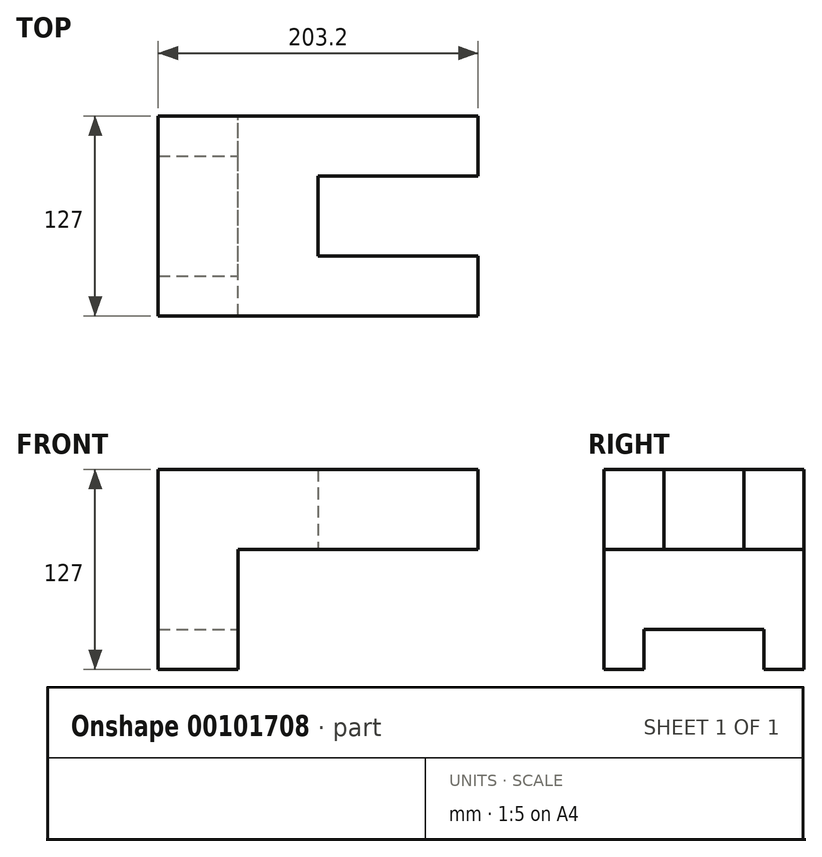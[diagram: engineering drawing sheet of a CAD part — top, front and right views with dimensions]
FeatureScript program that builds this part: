
annotation { "Feature Type Name" : "Feature", "Feature Type Description" : "" }
export const myFeature = defineFeature(function(context is Context, id is Id, definition is map)
    precondition{}
    {
        {
            var Q0;
            Q0=qCreatedBy(makeId("Top.planeOp"),FACE);
            var sketch = newSketch(context, id + "F0", { "sketchPlane" : qUnion([Q0])});
            skLineSegment(sketch, "E0", {"start": v(-106.5, 62.7) * mm, "end": v(96.7, 62.7) * mm});
            skLineSegment(sketch, "E1", {"start": v(96.7, 62.7) * mm, "end": v(96.7, 24.6) * mm});
            skLineSegment(sketch, "E2", {"start": v(96.7, 24.6) * mm, "end": v(-4.9, 24.6) * mm});
            skLineSegment(sketch, "E3", {"start": v(-4.9, 24.6) * mm, "end": v(-4.9, -26.2) * mm});
            skLineSegment(sketch, "E4", {"start": v(-4.9, -26.2) * mm, "end": v(96.7, -26.2) * mm});
            skLineSegment(sketch, "E5", {"start": v(96.7, -26.2) * mm, "end": v(96.7, -64.3) * mm});
            skLineSegment(sketch, "E6", {"start": v(-106.5, 62.7) * mm, "end": v(-106.5, -64.3) * mm});
            skLineSegment(sketch, "E7", {"start": v(-106.5, -64.3) * mm, "end": v(96.7, -64.3) * mm});
            skSolve(sketch);
        }
        {
            var Q0;
            Q0 = qSketchRegion(id + "F0", true);
            var Q1;
            Q1=makeQuery(id+"F0.imprint","IMPRINT",FACE,{"disambiguationData":[TD([[makeQuery(id+"F0.imprint","IMPRINT",EDGE,{"derivedFrom":sQuery(id+"F0.wireOp",EDGE,"E0")}),-1.0]])]});
            extrude(context, id + "F1", {"entities" : qUnion([Q0, Q1]), "depth" : 50.8 * mm});
        }
        {
            var Q0;
            Q0=makeQuery(id+"F1.opExtrude","CAP_FACE",FACE,{"disambiguationData":[OSD([sQuery(id+"F0.wireOp",EDGE,"E0"),sQuery(id+"F0.wireOp",EDGE,"E1"),sQuery(id+"F0.wireOp",EDGE,"E2"),sQuery(id+"F0.wireOp",EDGE,"E3"),sQuery(id+"F0.wireOp",EDGE,"E4"),sQuery(id+"F0.wireOp",EDGE,"E5"),sQuery(id+"F0.wireOp",EDGE,"E6"),sQuery(id+"F0.wireOp",EDGE,"E7")])],"isStart":true});
            var sketch = newSketch(context, id + "F2", { "sketchPlane" : qUnion([Q0])});
            skLineSegment(sketch, "E8.bottom", {"start": v(-106.5, 64.3) * mm, "end": v(-55.7, 64.3) * mm});
            skLineSegment(sketch, "E8.top", {"start": v(-106.5, -62.7) * mm, "end": v(-55.7, -62.7) * mm});
            skLineSegment(sketch, "E8.left", {"start": v(-106.5, 64.3) * mm, "end": v(-106.5, -62.7) * mm});
            skLineSegment(sketch, "E8.right", {"start": v(-55.7, 64.3) * mm, "end": v(-55.7, -62.7) * mm});
            skSolve(sketch);
        }
        {
            var Q0;
            Q0=makeQuery(id+"F2.imprint","IMPRINT",FACE,{"disambiguationData":[TD([[makeQuery(id+"F2.imprint","IMPRINT",EDGE,{"derivedFrom":sQuery(id+"F2.wireOp",EDGE,"E8.bottom")}),-1.0]])]});
            extrude(context, id + "F3", {"entities" : qUnion([Q0]), "operationType" : NewBodyOperationType.ADD, "depth" : 50.8 * mm});
        }
        {
            var Q0;
            Q0=makeQuery(id+"F3.opExtrude","CAP_FACE",FACE,{"disambiguationData":[OSD([sQuery(id+"F2.wireOp",EDGE,"E8.bottom"),sQuery(id+"F2.wireOp",EDGE,"E8.top"),sQuery(id+"F2.wireOp",EDGE,"E8.left"),sQuery(id+"F2.wireOp",EDGE,"E8.right")])],"isStart":false});
            var sketch = newSketch(context, id + "F4", { "sketchPlane" : qUnion([Q0])});
            skLineSegment(sketch, "E9.bottom", {"start": v(-106.5, -62.7) * mm, "end": v(-55.7, -62.7) * mm});
            skLineSegment(sketch, "E9.top", {"start": v(-106.5, -37.3) * mm, "end": v(-55.7, -37.3) * mm});
            skLineSegment(sketch, "E9.left", {"start": v(-106.5, -62.7) * mm, "end": v(-106.5, -37.3) * mm});
            skLineSegment(sketch, "E9.right", {"start": v(-55.7, -62.7) * mm, "end": v(-55.7, -37.3) * mm});
            skSolve(sketch);
        }
        {
            var Q0;
            Q0=makeQuery(id+"F4.imprint","IMPRINT",FACE,{"disambiguationData":[TD([[makeQuery(id+"F4.imprint","IMPRINT",EDGE,{"derivedFrom":sQuery(id+"F4.wireOp",EDGE,"E9.bottom")}),1.0]])]});
            extrude(context, id + "F5", {"entities" : qUnion([Q0]), "operationType" : NewBodyOperationType.ADD, "depth" : 25.4 * mm});
        }
        {
            var Q0;
            Q0=makeQuery(id+"F3.opExtrude","CAP_FACE",FACE,{"disambiguationData":[OSD([sQuery(id+"F2.wireOp",EDGE,"E8.bottom"),sQuery(id+"F2.wireOp",EDGE,"E8.top"),sQuery(id+"F2.wireOp",EDGE,"E8.left"),sQuery(id+"F2.wireOp",EDGE,"E8.right")])],"isStart":false});
            var sketch = newSketch(context, id + "F6", { "sketchPlane" : qUnion([Q0])});
            skLineSegment(sketch, "E10.bottom", {"start": v(-106.5, 64.3) * mm, "end": v(-55.7, 64.3) * mm});
            skLineSegment(sketch, "E10.top", {"start": v(-106.5, 38.9) * mm, "end": v(-55.7, 38.9) * mm});
            skLineSegment(sketch, "E10.left", {"start": v(-106.5, 64.3) * mm, "end": v(-106.5, 38.9) * mm});
            skLineSegment(sketch, "E10.right", {"start": v(-55.7, 64.3) * mm, "end": v(-55.7, 38.9) * mm});
            skSolve(sketch);
        }
        {
            var Q0;
            Q0=makeQuery(id+"F6.imprint","IMPRINT",FACE,{"disambiguationData":[TD([[makeQuery(id+"F6.imprint","IMPRINT",EDGE,{"derivedFrom":sQuery(id+"F6.wireOp",EDGE,"E10.bottom")}),-1.0]])]});
            extrude(context, id + "F7", {"entities" : qUnion([Q0]), "operationType" : NewBodyOperationType.ADD, "depth" : 25.4 * mm});
        }
    });
